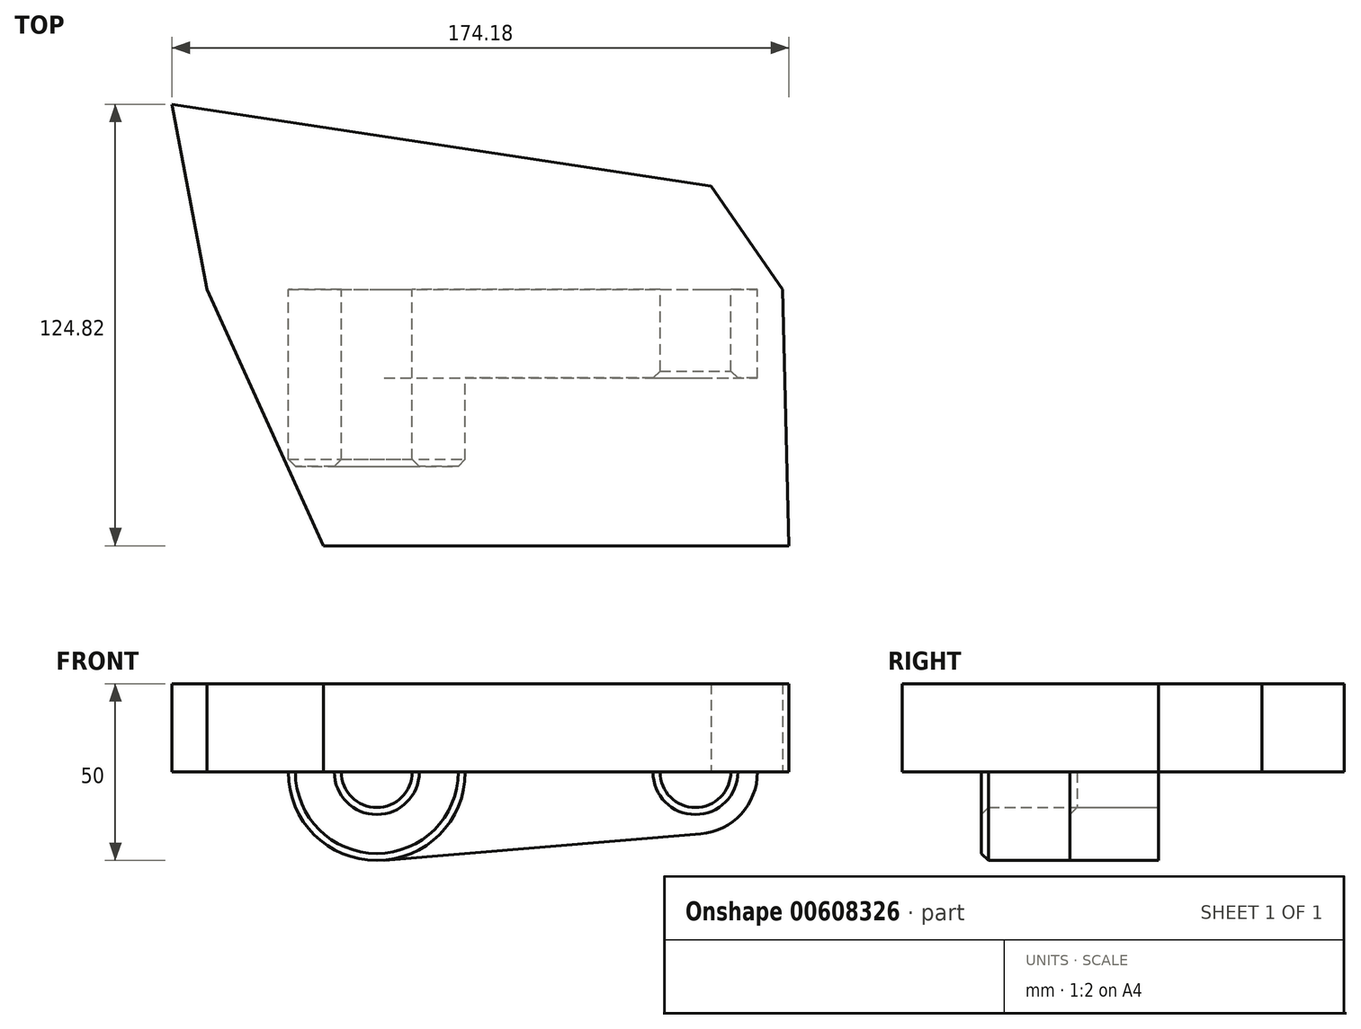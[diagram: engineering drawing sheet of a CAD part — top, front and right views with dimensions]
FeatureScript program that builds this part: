
annotation { "Feature Type Name" : "Feature", "Feature Type Description" : "" }
export const myFeature = defineFeature(function(context is Context, id is Id, definition is map)
    precondition{}
    {
        {
            var Q0;
            Q0=qCreatedBy(makeId("Front.planeOp"),FACE);
            var sketch = newSketch(context, id + "F0", { "sketchPlane" : qUnion([Q0])});
            skCircle(sketch, "E0", {"center": v(0, 0) * mm, "radius": 25 * mm});
            skCircle(sketch, "E1", {"center": v(90, 0) * mm, "radius": 17.5 * mm});
            skLineSegment(sketch, "E2", {"start": v(2.08, 24.91) * mm, "end": v(91.46, 17.44) * mm});
            skLineSegment(sketch, "E3", {"start": v(2.08, -24.91) * mm, "end": v(91.46, -17.44) * mm});
            skCircle(sketch, "E4", {"center": v(0, 0) * mm, "radius": 10 * mm});
            skCircle(sketch, "E5", {"center": v(90, 0) * mm, "radius": 10 * mm});
            skSolve(sketch);
        }
        {
            var Q0;
            Q0=qSketchRegion(id+"F0",true);
            extrude(context, id + "F1", {"entities" : qUnion([Q0]), "depth" : 25 * mm});
        }
        {
            var Q0;
            Q0=makeQuery(id+"F0.imprint","IMPRINT",FACE,{"disambiguationData":[TD([[makeQuery(id+"F0.imprint","IMPRINT",EDGE,{"derivedFrom":sQuery(id+"F0.wireOp",EDGE,"E4")}),-1.0]])]});
            extrude(context, id + "F2", {"entities" : qUnion([Q0]), "operationType" : NewBodyOperationType.ADD, "depth" : 50 * mm});
        }
        {
            var Q0;
            Q0=makeQuery(id+"F2.opExtrude","CAP_EDGE",EDGE,{"disambiguationData":[OSD([sQuery(id+"F0.wireOp",EDGE,"E0")])],"isStart":false});
            var Q1;
            Q1=makeQuery(id+"F2.opExtrude","CAP_EDGE",EDGE,{"disambiguationData":[OSD([sQuery(id+"F0.wireOp",EDGE,"E4")])],"isStart":false});
            var Q2;
            Q2=makeQuery(id+"F1.opExtrude","CAP_EDGE",EDGE,{"disambiguationData":[OSD([sQuery(id+"F0.wireOp",EDGE,"E5")])],"isStart":false});
            chamfer(context, id + "F3", {"entities" : qUnion([Q0, Q1, Q2]), "width" : 2 * mm, "tangentPropagation" : true});
        }
        {
            var Q0;
            Q0=qCreatedBy(makeId("Top.planeOp"),FACE);
            var sketch = newSketch(context, id + "F4", { "sketchPlane" : qUnion([Q0])});
            skLineSegment(sketch, "E6", {"start": v(-44.6, 79.75) * mm, "end": v(101.8, 79.75) * mm});
            skLineSegment(sketch, "E7", {"start": v(101.8, 79.75) * mm, "end": v(74.3, 58.42) * mm});
            skLineSegment(sketch, "E8", {"start": v(74.3, 58.42) * mm, "end": v(74.3, 58.42) * mm});
            skLineSegment(sketch, "E9", {"start": v(114.55, 0) * mm, "end": v(74.3, 58.42) * mm});
            skLineSegment(sketch, "E10", {"start": v(-71.04, 79.75) * mm, "end": v(-71.04, 100.04) * mm});
            skLineSegment(sketch, "E11", {"start": v(-71.04, 100.04) * mm, "end": v(-44.6, 79.75) * mm});
            skLineSegment(sketch, "E12", {"start": v(94.42, 29.21) * mm, "end": v(-57.82, 52.42) * mm});
            skPoint(sketch, "E12.endSnap0", {"position": v(-57.82, 89.9) * mm});
            skLineSegment(sketch, "E13", {"start": v(-57.82, 52.42) * mm, "end": v(-47.97, 0) * mm});
            skLineSegment(sketch, "E14", {"start": v(-47.97, 0) * mm, "end": v(-15.1, -72.4) * mm});
            skLineSegment(sketch, "E15", {"start": v(-15.1, -72.4) * mm, "end": v(116.36, -72.4) * mm});
            skLineSegment(sketch, "E16", {"start": v(116.36, -72.4) * mm, "end": v(114.55, 0) * mm});
            skSolve(sketch);
        }
        {
            var Q0;
            Q0 = qSketchRegion(id + "F4", true);
            extrude(context, id + "F5", {"entities" : qUnion([Q0]), "operationType" : NewBodyOperationType.ADD, "depth" : 25 * mm, "offsetDistance" : 25 * mm});
        }
    });
